# Revit family: Window
name_source: partatom
category: Windows
revit_build: Autodesk Revit 2014 (Build: 20130308_1515(x64)
units: mm (PartAtom-declared; Revit-internal decimal feet)

## types (1)
- Window
    1st Window Width = 880 mm  [stored 2.88714 ft]
    2nd Window Width = 880 mm  [stored 2.88714 ft]
    3rd Window Width = 880 mm  [stored 2.88714 ft]
    Analytic Construction = <None>
    Default Sill Height = 900 mm  [stored 2.95276 ft]
    Frame Depth = 150 mm
    Frame Material = Metal 16
    Glass Pane Material = Glass 01
    Height = 1200 mm
    Jamb Width = 40 mm  [stored 0.131234 ft]
    Lower Opening HEight = 1500 mm  [stored 4.92126 ft]
    Mullion Material = Metal 16
    Operable Frame Material = Metal 17
    Regular Mullion Width = 50 mm  [stored 0.164042 ft]
    Stopper Depth = 52 mm
    Stopper Inset = 16 mm
    Stopper Width = 19 mm  [stored 0.062336 ft]
    Upper Glass Material = Gray Panel
    Wall Closure = By host
    Width = 3910 mm  [stored 12.8281 ft]

note: [stored X ft] marks values corroborated as IEEE doubles in the binary element streams (Revit-internal decimal feet)

## geometry (parser evidence)
native form markers: Sweep x1
no freeform markers — native parametric forms only
